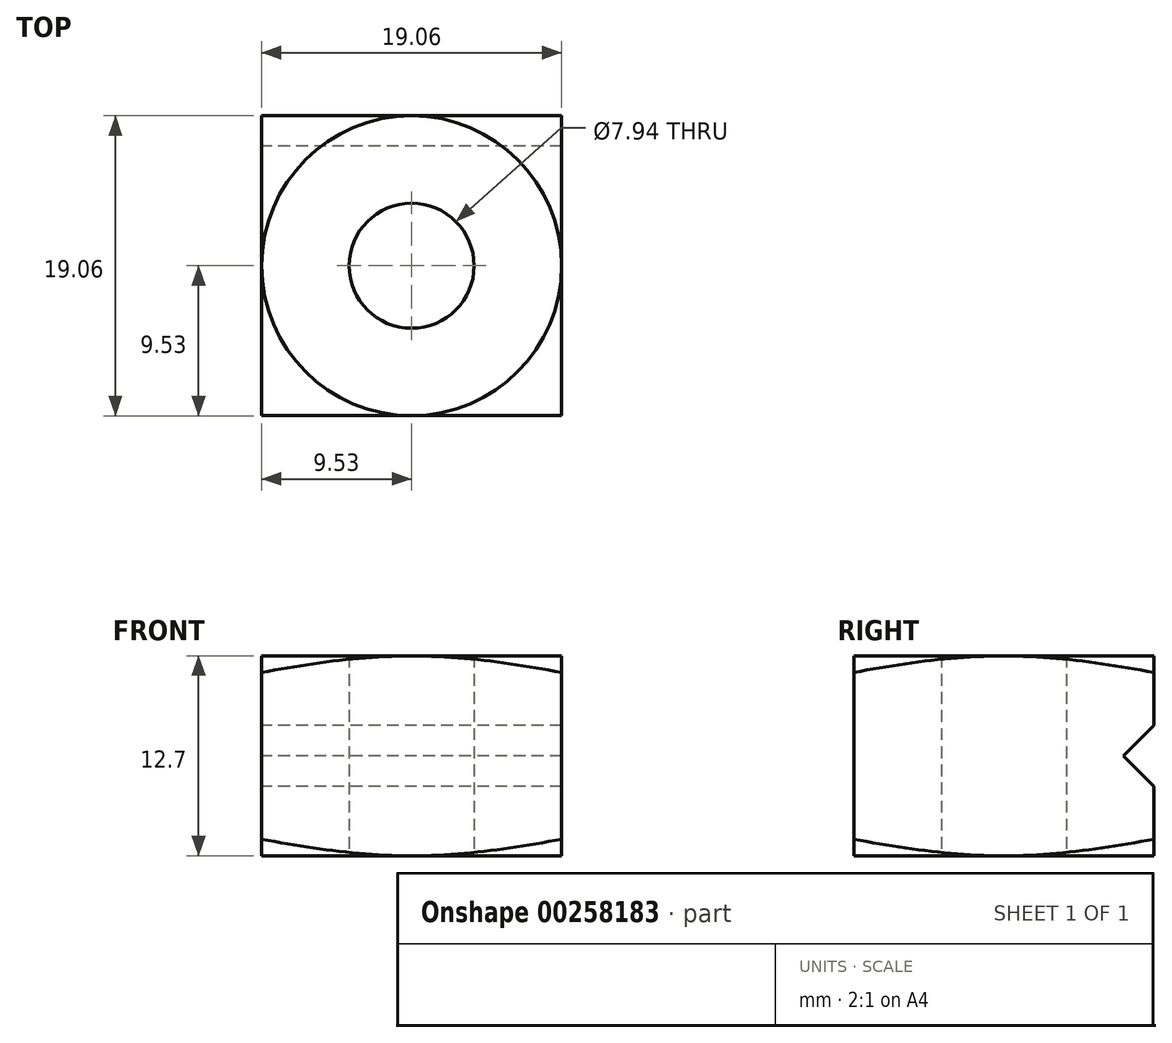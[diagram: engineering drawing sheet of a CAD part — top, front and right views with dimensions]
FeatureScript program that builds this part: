
annotation { "Feature Type Name" : "Feature", "Feature Type Description" : "" }
export const myFeature = defineFeature(function(context is Context, id is Id, definition is map)
    precondition{}
    {
        {
            var Q0;
            Q0=qCreatedBy(makeId("Top.planeOp"),FACE);
            var sketch = newSketch(context, id + "F0", { "sketchPlane" : qUnion([Q0])});
            skLineSegment(sketch, "E0.bottom", {"start": v(9.53, -9.52) * mm, "end": v(-9.53, -9.52) * mm});
            skLineSegment(sketch, "E0.top", {"start": v(9.53, 9.53) * mm, "end": v(-9.52, 9.53) * mm});
            skLineSegment(sketch, "E0.left", {"start": v(9.53, -9.52) * mm, "end": v(9.53, 9.53) * mm});
            skLineSegment(sketch, "E0.right", {"start": v(-9.53, -9.53) * mm, "end": v(-9.52, 9.53) * mm});
            skPoint(sketch, "E0.middle", {"position": v(0, 0) * mm});
            skCircle(sketch, "E1", {"center": v(0, 0) * mm, "radius": 3.97 * mm});
            skSolve(sketch);
        }
        {
            var Q0;
            Q0 = qSketchRegion(id + "F0", true);
            extrude(context, id + "F1", {"entities" : qUnion([Q0]), "depth" : 6.35 * mm});
        }
        {
            var Q0;
            Q0=makeQuery(id+"F1.opExtrude","CAP_FACE",FACE,{"disambiguationData":[OSD([sQuery(id+"F0.wireOp",EDGE,"E0.bottom"),sQuery(id+"F0.wireOp",EDGE,"E0.top"),sQuery(id+"F0.wireOp",EDGE,"E0.left"),sQuery(id+"F0.wireOp",EDGE,"E0.right"),sQuery(id+"F0.wireOp",EDGE,"E1")])],"isStart":true});
            var sketch = newSketch(context, id + "F2", { "sketchPlane" : qUnion([Q0])});
            skCircle(sketch, "E2", {"center": v(0, 0) * mm, "radius": 9.53 * mm});
            skSolve(sketch);
        }
        {
            var Q0;
            Q0=qCreatedBy(makeId("Right.planeOp"),FACE);
            var sketch = newSketch(context, id + "F3", { "sketchPlane" : qUnion([Q0])});
            skLineSegment(sketch, "E3.0.0", {"start": v(9.53, 0) * mm, "end": v(-9.52, 0) * mm});
            skLineSegment(sketch, "E3.0.2", {"start": v(-9.52, 0) * mm, "end": v(9.53, 0) * mm});
            skLineSegment(sketch, "E4", {"start": v(-9.52, 0) * mm, "end": v(-20.8, 0) * mm});
            skLineSegment(sketch, "E5", {"start": v(-20.8, 0) * mm, "end": v(-20.8, 3.02) * mm});
            skLineSegment(sketch, "E6", {"start": v(-20.8, 3.02) * mm, "end": v(-9.52, 0) * mm});
            skSolve(sketch);
        }
        {
            var Q0;
            Q0=makeQuery(id+"F3.imprint","IMPRINT",FACE,{"disambiguationData":[TD([[makeQuery(id+"F3.imprint","IMPRINT",EDGE,{"derivedFrom":sQuery(id+"F3.wireOp",EDGE,"E4")}),-1.0]])]});
            var Q1;
            Q1=sQuery(id+"F2.wireOp",EDGE,"E2");
            sweep(context, id + "F4", {"operationType" : NewBodyOperationType.REMOVE, "profiles" : qUnion([Q0]), "path" : qUnion([Q1])});
        }
        {
            var Q0;
            Q0=makeQuery(id+"F1.opExtrude","SWEPT_FACE",FACE,{"disambiguationData":[OSD([sQuery(id+"F0.wireOp",EDGE,"E0.right")])]});
            var sketch = newSketch(context, id + "F5", { "sketchPlane" : qUnion([Q0])});
            skLineSegment(sketch, "E7", {"start": v(-9.53, 6.35) * mm, "end": v(-7.6, 6.35) * mm});
            skLineSegment(sketch, "E8", {"start": v(-7.6, 6.35) * mm, "end": v(-9.53, 4.42) * mm});
            skLineSegment(sketch, "E9", {"start": v(-9.53, 4.42) * mm, "end": v(-9.53, 6.35) * mm});
            skSolve(sketch);
        }
        {
            var Q0;
            Q0=makeQuery(id+"F5.imprint","IMPRINT",FACE,{"disambiguationData":[TD([[makeQuery(id+"F5.imprint","IMPRINT",EDGE,{"derivedFrom":sQuery(id+"F5.wireOp",EDGE,"E7")}),1.0]])]});
            extrude(context, id + "F6", {"entities" : qUnion([Q0]), "operationType" : NewBodyOperationType.REMOVE, "endBound" : BoundingType.THROUGH_ALL, "oppositeDirection" : true, "depth" : 25.4 * mm});
        }
        {
            var Q0;
            Q0=makeQuery(id+"F1.opExtrude","SWEPT_BODY",BODY,{"disambiguationData":[OSD([sQuery(id+"F0.wireOp",EDGE,"E0.bottom"),sQuery(id+"F0.wireOp",EDGE,"E0.top"),sQuery(id+"F0.wireOp",EDGE,"E0.left"),sQuery(id+"F0.wireOp",EDGE,"E0.right"),sQuery(id+"F0.wireOp",EDGE,"E1")])]});
            var Q1;
            Q1=makeQuery(id+"F1.opExtrude","CAP_FACE",FACE,{"disambiguationData":[OSD([sQuery(id+"F0.wireOp",EDGE,"E0.bottom"),sQuery(id+"F0.wireOp",EDGE,"E0.top"),sQuery(id+"F0.wireOp",EDGE,"E0.left"),sQuery(id+"F0.wireOp",EDGE,"E0.right"),sQuery(id+"F0.wireOp",EDGE,"E1")])],"isStart":false});
            mirror(context, id + "F7", {"operationType" : NewBodyOperationType.ADD, "entities" : qUnion([Q0]), "mirrorPlane" : qUnion([Q1])});
        }
    });
